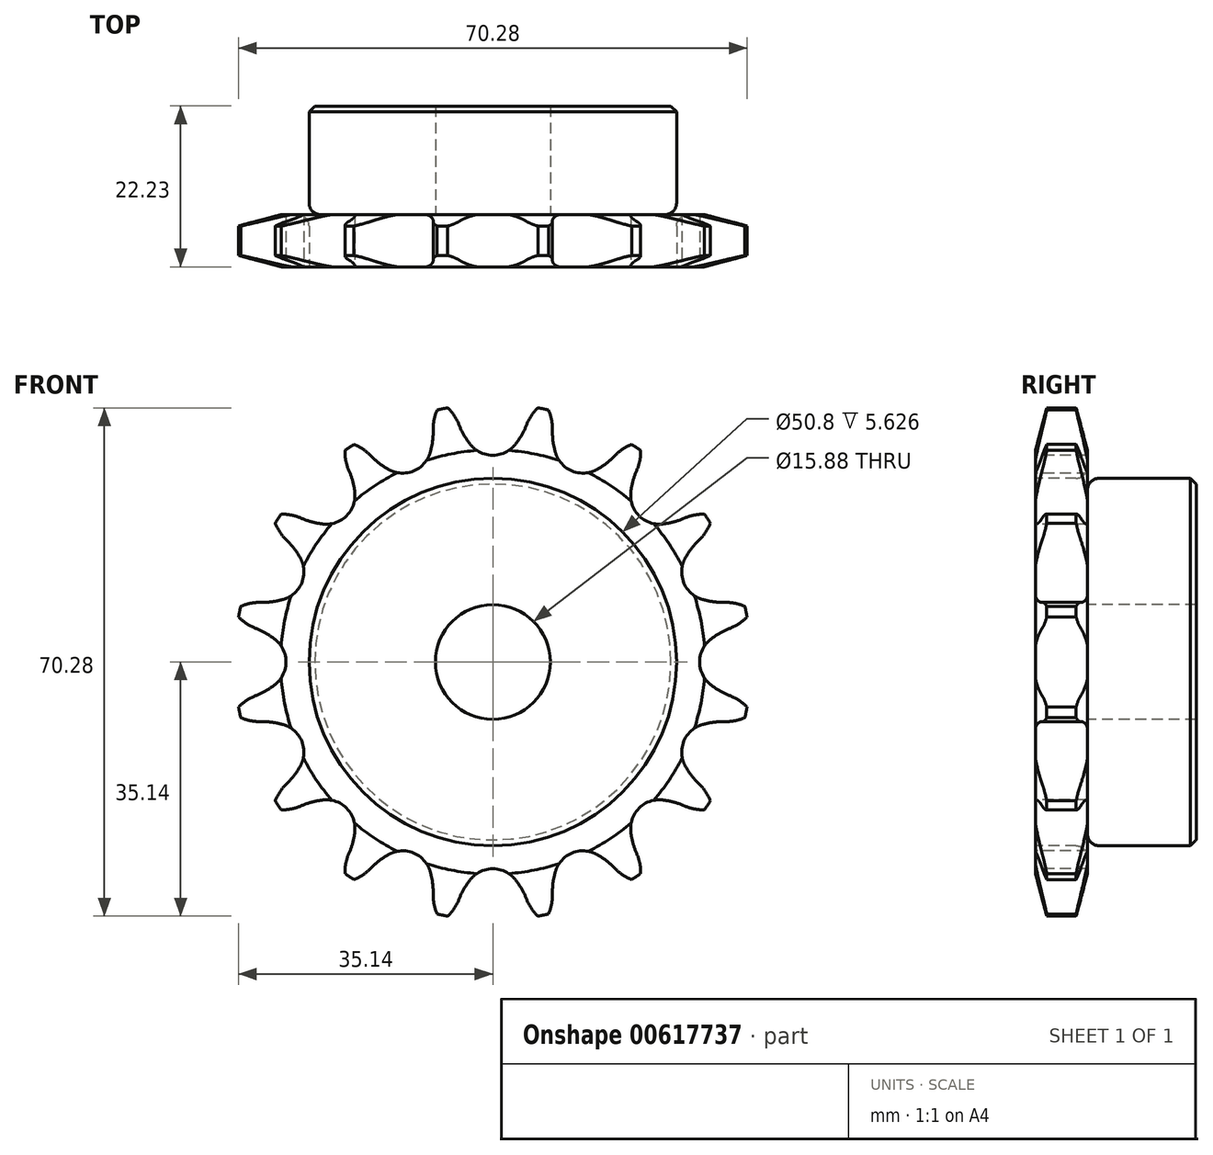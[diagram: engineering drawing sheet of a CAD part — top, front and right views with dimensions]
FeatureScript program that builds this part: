
annotation { "Feature Type Name" : "Feature", "Feature Type Description" : "" }
export const myFeature = defineFeature(function(context is Context, id is Id, definition is map)
    precondition{}
    {
        {
            var Q0;
            Q0=qCreatedBy(makeId("Right.planeOp"),FACE);
            var sketch = newSketch(context, id + "F0", { "sketchPlane" : qUnion([Q0])});
            skLineSegment(sketch, "E0", {"start": v(0, 0) * mm, "end": v(26.74, 0) * mm, "construction": true});
            skLineSegment(sketch, "E1.bottom", {"start": v(0, 7.94) * mm, "end": v(7.21, 7.94) * mm});
            skLineSegment(sketch, "E1.top", {"start": v(0, 35.69) * mm, "end": v(7.21, 35.69) * mm});
            skLineSegment(sketch, "E1.left", {"start": v(0, 7.94) * mm, "end": v(0, 35.69) * mm});
            skLineSegment(sketch, "E1.right", {"start": v(7.21, 7.94) * mm, "end": v(7.21, 35.69) * mm});
            skLineSegment(sketch, "E2.bottom", {"start": v(0, 7.94) * mm, "end": v(22.23, 7.94) * mm});
            skLineSegment(sketch, "E2.top", {"start": v(0, 25.4) * mm, "end": v(22.23, 25.4) * mm});
            skLineSegment(sketch, "E2.left", {"start": v(0, 7.94) * mm, "end": v(0, 25.4) * mm});
            skLineSegment(sketch, "E2.right", {"start": v(22.23, 7.94) * mm, "end": v(22.22, 25.4) * mm});
            skLineSegment(sketch, "E3.MirrorCS", {"start": v(0, -7.94) * mm, "end": v(7.21, -7.94) * mm});
            skLineSegment(sketch, "E4.MirrorCS", {"start": v(22.23, -7.94) * mm, "end": v(22.23, -25.4) * mm});
            skLineSegment(sketch, "E5.MirrorCS", {"start": v(0, -7.94) * mm, "end": v(0, -25.4) * mm});
            skLineSegment(sketch, "E6.MirrorCS", {"start": v(0, -35.69) * mm, "end": v(7.21, -35.69) * mm});
            skLineSegment(sketch, "E7.MirrorCS", {"start": v(0, -7.94) * mm, "end": v(0, -35.69) * mm});
            skLineSegment(sketch, "E8.MirrorCS", {"start": v(7.21, -7.94) * mm, "end": v(7.21, -35.69) * mm});
            skLineSegment(sketch, "E9.MirrorCS", {"start": v(0, -7.94) * mm, "end": v(22.23, -7.94) * mm});
            skLineSegment(sketch, "E10.MirrorCS", {"start": v(0, -25.4) * mm, "end": v(22.23, -25.4) * mm});
            skSolve(sketch);
        }
        {
            var Q0;
            {var subQ0=sQuery(id+"F0.wireOp",EDGE,"E1.top");Q0=makeQuery(id+"F0.imprint","IMPRINT",FACE,{"disambiguationData":[TD([[makeQuery(id+"F0.imprint","IMPRINT",EDGE,{"derivedFrom":subQ0}),-1.0]])]});}
            var Q1;
            {var subQ5=sQuery(id+"F0.wireOp",EDGE,"E2.left");Q1=makeQuery(id+"F0.imprint","IMPRINT",FACE,{"disambiguationData":[TD([[makeQuery(id+"F0.imprint","IMPRINT",EDGE,{"derivedFrom":subQ5}),-1.0]])]});}
            var Q2;
            {var subQ5=sQuery(id+"F0.wireOp",EDGE,"E2.right");Q2=makeQuery(id+"F0.imprint","IMPRINT",FACE,{"disambiguationData":[TD([[makeQuery(id+"F0.imprint","IMPRINT",EDGE,{"derivedFrom":subQ5}),1.0]])]});}
            var Q3;
            Q3=sQuery(id+"F0.wireOp",EDGE,"E0");
            revolve(context, id + "F1", {"entities" : qUnion([Q0, Q1, Q2]), "axis" : qUnion([Q3]), "revolveType" : RevolveType.FULL});
        }
        {
            var Q0;
            Q0=makeQuery(id+"F1.opRevolve","SWEPT_EDGE",EDGE,{"disambiguationData":[OSD([sQuery(id+"F0.wireOp",EDGE,"E1.right"),sQuery(id+"F0.wireOp",EDGE,"E2.top")])]});
            fillet(context, id + "F2", {"entities" : qUnion([Q0]), "radius" : 1.59 * mm, "tangentPropagation" : true, "allowEdgeOverflow" : false});
        }
        {
            var Q0;
            Q0=makeQuery(id+"F1.opRevolve","SWEPT_EDGE",EDGE,{"disambiguationData":[OSD([sQuery(id+"F0.wireOp",EDGE,"E2.top"),sQuery(id+"F0.wireOp",EDGE,"E2.right")])]});
            chamfer(context, id + "F3", {"entities" : qUnion([Q0]), "width" : 0.8 * mm, "tangentPropagation" : true});
        }
        {
            var Q0;
            Q0=makeQuery(id+"F1.opRevolve","SWEPT_FACE",FACE,{"disambiguationData":[OSD([sQuery(id+"F0.wireOp",EDGE,"E1.top")])]});
            chamfer(context, id + "F4", {"entities" : qUnion([Q0]), "chamferType" : ChamferType.TWO_OFFSETS, "width1" : 6.35 * mm, "oppositeDirection" : false, "width2" : 1.57 * mm, "tangentPropagation" : true});
        }
        {
            var Q0;
            Q0=makeQuery(id+"F1.opRevolve","SWEPT_FACE",FACE,{"disambiguationData":[OSD([sQuery(id+"F0.wireOp",EDGE,"E1.left"),sQuery(id+"F0.wireOp",EDGE,"E2.left")])]});
            var sketch = newSketch(context, id + "F5", { "sketchPlane" : qUnion([Q0])});
            skLineSegment(sketch, "E11", {"start": v(0, 0) * mm, "end": v(0, 32.55) * mm, "construction": true});
            skLineSegment(sketch, "E12", {"start": v(0, 32.55) * mm, "end": v(33.66, 32.55) * mm, "construction": true});
            skLineSegment(sketch, "E13", {"start": v(0, 32.55) * mm, "end": v(5, 36.56) * mm, "construction": true});
            skLineSegment(sketch, "E14", {"start": v(5, 36.56) * mm, "end": v(-3.9, 32.55) * mm, "construction": true});
            skLineSegment(sketch, "E15", {"start": v(3.62, 15.85) * mm, "end": v(-3.9, 32.55) * mm, "construction": true});
            skArc(sketch, "E16", {"start": v(-7.13, 35.87) * mm, "mid": v(-15.94, 26.26) * mm, "end": v(-4.66, 32.79) * mm, "construction": true});
            skArc(sketch, "E17", {"start": v(-4.66, 32.79) * mm, "mid": v(-5.66, 34.52) * mm, "end": v(-7.13, 35.87) * mm});
            skLineSegment(sketch, "E18", {"start": v(-4.66, 32.79) * mm, "end": v(-4.66, 32.79) * mm});
            skArc(sketch, "E19", {"start": v(-3.1, 30.07) * mm, "mid": v(-1.71, 28.98) * mm, "end": v(0, 28.59) * mm});
            skArc(sketch, "E20", {"start": v(-4.66, 32.79) * mm, "mid": v(-3.98, 31.37) * mm, "end": v(-3.1, 30.07) * mm});
            skArc(sketch, "E21.MirrorCS", {"start": v(4.66, 32.79) * mm, "mid": v(5.66, 34.52) * mm, "end": v(7.13, 35.87) * mm});
            skArc(sketch, "E22.MirrorCS", {"start": v(4.66, 32.79) * mm, "mid": v(3.98, 31.37) * mm, "end": v(3.1, 30.07) * mm});
            skArc(sketch, "E23.MirrorCS", {"start": v(3.1, 30.07) * mm, "mid": v(1.71, 28.98) * mm, "end": v(0, 28.59) * mm});
            skArc(sketch, "E24.1.0", {"start": v(-16.85, 28.5) * mm, "mid": v(-18.44, 29.72) * mm, "end": v(-20.32, 30.4) * mm});
            skArc(sketch, "E24.1.1", {"start": v(-16.85, 28.5) * mm, "mid": v(-15.68, 27.46) * mm, "end": v(-14.36, 26.6) * mm});
            skArc(sketch, "E24.1.2", {"start": v(-14.36, 26.6) * mm, "mid": v(-12.67, 26.12) * mm, "end": v(-10.94, 26.41) * mm});
            skArc(sketch, "E24.1.3", {"start": v(-8.65, 28.96) * mm, "mid": v(-9.5, 27.43) * mm, "end": v(-10.94, 26.41) * mm});
            skArc(sketch, "E24.1.4", {"start": v(-8.24, 32.08) * mm, "mid": v(-8.33, 30.5) * mm, "end": v(-8.65, 28.96) * mm});
            skArc(sketch, "E24.1.5", {"start": v(-8.24, 32.08) * mm, "mid": v(-7.98, 34.06) * mm, "end": v(-7.13, 35.87) * mm});
            skArc(sketch, "E24.2.0", {"start": v(-26.48, 19.89) * mm, "mid": v(-28.41, 20.4) * mm, "end": v(-30.4, 20.32) * mm});
            skArc(sketch, "E24.2.1", {"start": v(-26.48, 19.89) * mm, "mid": v(-25, 19.37) * mm, "end": v(-23.45, 19.08) * mm});
            skArc(sketch, "E24.2.2", {"start": v(-23.45, 19.08) * mm, "mid": v(-21.7, 19.28) * mm, "end": v(-20.21, 20.21) * mm});
            skArc(sketch, "E24.2.3", {"start": v(-19.08, 23.45) * mm, "mid": v(-19.28, 21.7) * mm, "end": v(-20.21, 20.21) * mm});
            skArc(sketch, "E24.2.4", {"start": v(-19.89, 26.48) * mm, "mid": v(-19.37, 25) * mm, "end": v(-19.08, 23.45) * mm});
            skArc(sketch, "E24.2.5", {"start": v(-19.89, 26.48) * mm, "mid": v(-20.4, 28.41) * mm, "end": v(-20.32, 30.4) * mm});
            skArc(sketch, "E24.3.0", {"start": v(-32.08, 8.24) * mm, "mid": v(-34.06, 7.98) * mm, "end": v(-35.87, 7.13) * mm});
            skArc(sketch, "E24.3.1", {"start": v(-32.08, 8.24) * mm, "mid": v(-30.5, 8.33) * mm, "end": v(-28.96, 8.65) * mm});
            skArc(sketch, "E24.3.2", {"start": v(-28.96, 8.65) * mm, "mid": v(-27.43, 9.5) * mm, "end": v(-26.41, 10.94) * mm});
            skArc(sketch, "E24.3.3", {"start": v(-26.6, 14.36) * mm, "mid": v(-26.12, 12.67) * mm, "end": v(-26.41, 10.94) * mm});
            skArc(sketch, "E24.3.4", {"start": v(-28.5, 16.85) * mm, "mid": v(-27.46, 15.68) * mm, "end": v(-26.6, 14.36) * mm});
            skArc(sketch, "E24.3.5", {"start": v(-28.5, 16.85) * mm, "mid": v(-29.72, 18.44) * mm, "end": v(-30.4, 20.32) * mm});
            skArc(sketch, "E24.4.0", {"start": v(-32.79, -4.66) * mm, "mid": v(-34.52, -5.66) * mm, "end": v(-35.87, -7.13) * mm});
            skArc(sketch, "E24.4.1", {"start": v(-32.79, -4.66) * mm, "mid": v(-31.37, -3.98) * mm, "end": v(-30.07, -3.1) * mm});
            skArc(sketch, "E24.4.2", {"start": v(-30.07, -3.1) * mm, "mid": v(-28.98, -1.71) * mm, "end": v(-28.59, 0) * mm});
            skArc(sketch, "E24.4.3", {"start": v(-30.07, 3.1) * mm, "mid": v(-28.98, 1.71) * mm, "end": v(-28.59, 0) * mm});
            skArc(sketch, "E24.4.4", {"start": v(-32.79, 4.66) * mm, "mid": v(-31.37, 3.98) * mm, "end": v(-30.07, 3.1) * mm});
            skArc(sketch, "E24.4.5", {"start": v(-32.79, 4.66) * mm, "mid": v(-34.52, 5.66) * mm, "end": v(-35.87, 7.13) * mm});
            skArc(sketch, "E24.5.0", {"start": v(-28.5, -16.85) * mm, "mid": v(-29.72, -18.44) * mm, "end": v(-30.4, -20.32) * mm});
            skArc(sketch, "E24.5.1", {"start": v(-28.5, -16.85) * mm, "mid": v(-27.46, -15.68) * mm, "end": v(-26.6, -14.36) * mm});
            skArc(sketch, "E24.5.2", {"start": v(-26.6, -14.36) * mm, "mid": v(-26.12, -12.67) * mm, "end": v(-26.41, -10.94) * mm});
            skArc(sketch, "E24.5.3", {"start": v(-28.96, -8.65) * mm, "mid": v(-27.43, -9.5) * mm, "end": v(-26.41, -10.94) * mm});
            skArc(sketch, "E24.5.4", {"start": v(-32.08, -8.24) * mm, "mid": v(-30.5, -8.33) * mm, "end": v(-28.96, -8.65) * mm});
            skArc(sketch, "E24.5.5", {"start": v(-32.08, -8.24) * mm, "mid": v(-34.06, -7.98) * mm, "end": v(-35.87, -7.13) * mm});
            skArc(sketch, "E24.6.0", {"start": v(-19.89, -26.48) * mm, "mid": v(-20.4, -28.41) * mm, "end": v(-20.32, -30.4) * mm});
            skArc(sketch, "E24.6.1", {"start": v(-19.89, -26.48) * mm, "mid": v(-19.37, -25) * mm, "end": v(-19.08, -23.45) * mm});
            skArc(sketch, "E24.6.2", {"start": v(-19.08, -23.45) * mm, "mid": v(-19.28, -21.7) * mm, "end": v(-20.21, -20.21) * mm});
            skArc(sketch, "E24.6.3", {"start": v(-23.45, -19.08) * mm, "mid": v(-21.7, -19.28) * mm, "end": v(-20.21, -20.21) * mm});
            skArc(sketch, "E24.6.4", {"start": v(-26.48, -19.89) * mm, "mid": v(-25, -19.37) * mm, "end": v(-23.45, -19.08) * mm});
            skArc(sketch, "E24.6.5", {"start": v(-26.48, -19.89) * mm, "mid": v(-28.41, -20.4) * mm, "end": v(-30.4, -20.32) * mm});
            skArc(sketch, "E24.7.0", {"start": v(-8.24, -32.08) * mm, "mid": v(-7.98, -34.06) * mm, "end": v(-7.13, -35.87) * mm});
            skArc(sketch, "E24.7.1", {"start": v(-8.24, -32.08) * mm, "mid": v(-8.33, -30.5) * mm, "end": v(-8.65, -28.96) * mm});
            skArc(sketch, "E24.7.2", {"start": v(-8.65, -28.96) * mm, "mid": v(-9.5, -27.43) * mm, "end": v(-10.94, -26.41) * mm});
            skArc(sketch, "E24.7.3", {"start": v(-14.36, -26.6) * mm, "mid": v(-12.67, -26.12) * mm, "end": v(-10.94, -26.41) * mm});
            skArc(sketch, "E24.7.4", {"start": v(-16.85, -28.5) * mm, "mid": v(-15.68, -27.46) * mm, "end": v(-14.36, -26.6) * mm});
            skArc(sketch, "E24.7.5", {"start": v(-16.85, -28.5) * mm, "mid": v(-18.44, -29.72) * mm, "end": v(-20.32, -30.4) * mm});
            skArc(sketch, "E24.8.0", {"start": v(4.66, -32.79) * mm, "mid": v(5.66, -34.52) * mm, "end": v(7.13, -35.87) * mm});
            skArc(sketch, "E24.8.1", {"start": v(4.66, -32.79) * mm, "mid": v(3.98, -31.37) * mm, "end": v(3.1, -30.07) * mm});
            skArc(sketch, "E24.8.2", {"start": v(3.1, -30.07) * mm, "mid": v(1.71, -28.98) * mm, "end": v(0, -28.59) * mm});
            skArc(sketch, "E24.8.3", {"start": v(-3.1, -30.07) * mm, "mid": v(-1.71, -28.98) * mm, "end": v(0, -28.59) * mm});
            skArc(sketch, "E24.8.4", {"start": v(-4.66, -32.79) * mm, "mid": v(-3.98, -31.37) * mm, "end": v(-3.1, -30.07) * mm});
            skArc(sketch, "E24.8.5", {"start": v(-4.66, -32.79) * mm, "mid": v(-5.66, -34.52) * mm, "end": v(-7.13, -35.87) * mm});
            skArc(sketch, "E24.9.0", {"start": v(16.85, -28.5) * mm, "mid": v(18.44, -29.72) * mm, "end": v(20.32, -30.4) * mm});
            skArc(sketch, "E24.9.1", {"start": v(16.85, -28.5) * mm, "mid": v(15.68, -27.46) * mm, "end": v(14.36, -26.6) * mm});
            skArc(sketch, "E24.9.2", {"start": v(14.36, -26.6) * mm, "mid": v(12.67, -26.12) * mm, "end": v(10.94, -26.41) * mm});
            skArc(sketch, "E24.9.3", {"start": v(8.65, -28.96) * mm, "mid": v(9.5, -27.43) * mm, "end": v(10.94, -26.41) * mm});
            skArc(sketch, "E24.9.4", {"start": v(8.24, -32.08) * mm, "mid": v(8.33, -30.5) * mm, "end": v(8.65, -28.96) * mm});
            skArc(sketch, "E24.9.5", {"start": v(8.24, -32.08) * mm, "mid": v(7.98, -34.06) * mm, "end": v(7.13, -35.87) * mm});
            skArc(sketch, "E24.10.0", {"start": v(26.48, -19.89) * mm, "mid": v(28.41, -20.4) * mm, "end": v(30.4, -20.32) * mm});
            skArc(sketch, "E24.10.1", {"start": v(26.48, -19.89) * mm, "mid": v(25, -19.37) * mm, "end": v(23.45, -19.08) * mm});
            skArc(sketch, "E24.10.2", {"start": v(23.45, -19.08) * mm, "mid": v(21.7, -19.28) * mm, "end": v(20.21, -20.21) * mm});
            skArc(sketch, "E24.10.3", {"start": v(19.08, -23.45) * mm, "mid": v(19.28, -21.7) * mm, "end": v(20.21, -20.21) * mm});
            skArc(sketch, "E24.10.4", {"start": v(19.89, -26.48) * mm, "mid": v(19.37, -25) * mm, "end": v(19.08, -23.45) * mm});
            skArc(sketch, "E24.10.5", {"start": v(19.89, -26.48) * mm, "mid": v(20.4, -28.41) * mm, "end": v(20.32, -30.4) * mm});
            skArc(sketch, "E24.11.0", {"start": v(32.08, -8.24) * mm, "mid": v(34.06, -7.98) * mm, "end": v(35.87, -7.13) * mm});
            skArc(sketch, "E24.11.1", {"start": v(32.08, -8.24) * mm, "mid": v(30.5, -8.33) * mm, "end": v(28.96, -8.65) * mm});
            skArc(sketch, "E24.11.2", {"start": v(28.96, -8.65) * mm, "mid": v(27.43, -9.5) * mm, "end": v(26.41, -10.94) * mm});
            skArc(sketch, "E24.11.3", {"start": v(26.6, -14.36) * mm, "mid": v(26.12, -12.67) * mm, "end": v(26.41, -10.94) * mm});
            skArc(sketch, "E24.11.4", {"start": v(28.5, -16.85) * mm, "mid": v(27.46, -15.68) * mm, "end": v(26.6, -14.36) * mm});
            skArc(sketch, "E24.11.5", {"start": v(28.5, -16.85) * mm, "mid": v(29.72, -18.44) * mm, "end": v(30.4, -20.32) * mm});
            skArc(sketch, "E24.12.0", {"start": v(32.79, 4.66) * mm, "mid": v(34.52, 5.66) * mm, "end": v(35.87, 7.13) * mm});
            skArc(sketch, "E24.12.1", {"start": v(32.79, 4.66) * mm, "mid": v(31.37, 3.98) * mm, "end": v(30.07, 3.1) * mm});
            skArc(sketch, "E24.12.2", {"start": v(30.07, 3.1) * mm, "mid": v(28.98, 1.71) * mm, "end": v(28.59, 0) * mm});
            skArc(sketch, "E24.12.3", {"start": v(30.07, -3.1) * mm, "mid": v(28.98, -1.71) * mm, "end": v(28.59, 0) * mm});
            skArc(sketch, "E24.12.4", {"start": v(32.79, -4.66) * mm, "mid": v(31.37, -3.98) * mm, "end": v(30.07, -3.1) * mm});
            skArc(sketch, "E24.12.5", {"start": v(32.79, -4.66) * mm, "mid": v(34.52, -5.66) * mm, "end": v(35.87, -7.13) * mm});
            skArc(sketch, "E24.13.0", {"start": v(28.5, 16.85) * mm, "mid": v(29.72, 18.44) * mm, "end": v(30.4, 20.32) * mm});
            skArc(sketch, "E24.13.1", {"start": v(28.5, 16.85) * mm, "mid": v(27.46, 15.68) * mm, "end": v(26.6, 14.36) * mm});
            skArc(sketch, "E24.13.2", {"start": v(26.6, 14.36) * mm, "mid": v(26.12, 12.67) * mm, "end": v(26.41, 10.94) * mm});
            skArc(sketch, "E24.13.3", {"start": v(28.96, 8.65) * mm, "mid": v(27.43, 9.5) * mm, "end": v(26.41, 10.94) * mm});
            skArc(sketch, "E24.13.4", {"start": v(32.08, 8.24) * mm, "mid": v(30.5, 8.33) * mm, "end": v(28.96, 8.65) * mm});
            skArc(sketch, "E24.13.5", {"start": v(32.08, 8.24) * mm, "mid": v(34.06, 7.98) * mm, "end": v(35.87, 7.13) * mm});
            skArc(sketch, "E24.14.0", {"start": v(19.89, 26.48) * mm, "mid": v(20.4, 28.41) * mm, "end": v(20.32, 30.4) * mm});
            skArc(sketch, "E24.14.1", {"start": v(19.89, 26.48) * mm, "mid": v(19.37, 25) * mm, "end": v(19.08, 23.45) * mm});
            skArc(sketch, "E24.14.2", {"start": v(19.08, 23.45) * mm, "mid": v(19.28, 21.7) * mm, "end": v(20.21, 20.21) * mm});
            skArc(sketch, "E24.14.3", {"start": v(23.45, 19.08) * mm, "mid": v(21.7, 19.28) * mm, "end": v(20.21, 20.21) * mm});
            skArc(sketch, "E24.14.4", {"start": v(26.48, 19.89) * mm, "mid": v(25, 19.37) * mm, "end": v(23.45, 19.08) * mm});
            skArc(sketch, "E24.14.5", {"start": v(26.48, 19.89) * mm, "mid": v(28.41, 20.4) * mm, "end": v(30.4, 20.32) * mm});
            skArc(sketch, "E24.15.0", {"start": v(8.24, 32.08) * mm, "mid": v(7.98, 34.06) * mm, "end": v(7.13, 35.87) * mm});
            skArc(sketch, "E24.15.1", {"start": v(8.24, 32.08) * mm, "mid": v(8.33, 30.5) * mm, "end": v(8.65, 28.96) * mm});
            skArc(sketch, "E24.15.2", {"start": v(8.65, 28.96) * mm, "mid": v(9.5, 27.43) * mm, "end": v(10.94, 26.41) * mm});
            skArc(sketch, "E24.15.3", {"start": v(14.36, 26.6) * mm, "mid": v(12.67, 26.12) * mm, "end": v(10.94, 26.41) * mm});
            skArc(sketch, "E24.15.4", {"start": v(16.85, 28.5) * mm, "mid": v(15.68, 27.46) * mm, "end": v(14.36, 26.6) * mm});
            skArc(sketch, "E24.15.5", {"start": v(16.85, 28.5) * mm, "mid": v(18.44, 29.72) * mm, "end": v(20.32, 30.4) * mm});
            skPoint(sketch, "E24.center", {"position": v(0, 0) * mm});
            skSolve(sketch);
        }
        {
            var Q0;
            Q0=qSketchRegion(id+"F5",true);
            extrude(context, id + "F6", {"entities" : qUnion([Q0]), "operationType" : NewBodyOperationType.INTERSECT, "endBound" : BoundingType.THROUGH_ALL, "oppositeDirection" : true, "depth" : 25.4 * mm});
        }
    });
